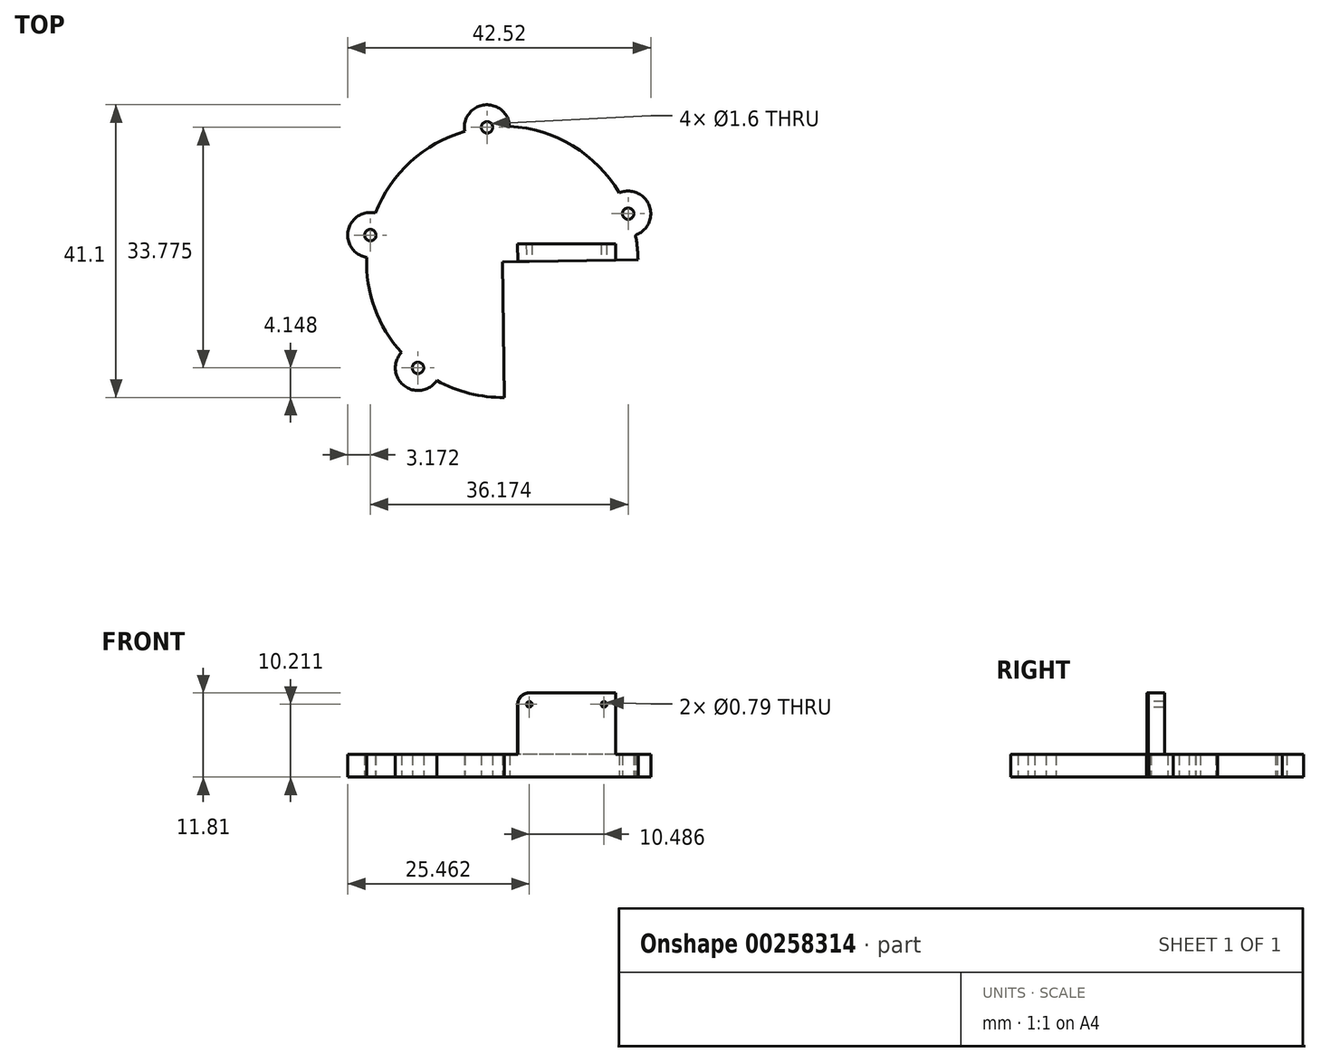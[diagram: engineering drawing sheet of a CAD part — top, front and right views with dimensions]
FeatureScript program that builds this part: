
annotation { "Feature Type Name" : "Feature", "Feature Type Description" : "" }
export const myFeature = defineFeature(function(context is Context, id is Id, definition is map)
    precondition{}
    {
        {
            var Q0;
            Q0=qCreatedBy(makeId("Top.planeOp"),FACE);
            var sketch = newSketch(context, id + "F0", { "sketchPlane" : qUnion([Q0])});
            skLineSegment(sketch, "E0", {"start": v(40.74, -31.1) * mm, "end": v(40.44, -12.05) * mm});
            skLineSegment(sketch, "E1", {"start": v(40.44, -12.05) * mm, "end": v(59.49, -11.75) * mm});
            skArc(sketch, "E2", {"start": v(59.49, -11.75) * mm, "mid": v(26.76, 1.2) * mm, "end": v(40.74, -31.1) * mm});
            skArc(sketch, "E3", {"start": v(26.28, -24.8) * mm, "mid": v(26.64, -29.44) * mm, "end": v(31.24, -28.73) * mm});
            skArc(sketch, "E4", {"start": v(22.66, -5.21) * mm, "mid": v(18.8, -7.67) * mm, "end": v(21.4, -11.43) * mm});
            skArc(sketch, "E5", {"start": v(41.47, 6.97) * mm, "mid": v(37.94, 9.98) * mm, "end": v(35.18, 6.26) * mm});
            skArc(sketch, "E6", {"start": v(59.12, -8.3) * mm, "mid": v(61.06, -4.16) * mm, "end": v(56.85, -2.38) * mm});
            skCircle(sketch, "E7", {"center": v(28.6, -26.95) * mm, "radius": 0.8 * mm});
            skCircle(sketch, "E8", {"center": v(21.92, -8.3) * mm, "radius": 0.8 * mm});
            skCircle(sketch, "E9", {"center": v(38.3, 6.82) * mm, "radius": 0.8 * mm});
            skCircle(sketch, "E10", {"center": v(58.1, -5.3) * mm, "radius": 0.8 * mm});
            skSolve(sketch);
        }
        {
            var Q0;
            Q0 = qSketchRegion(id + "F0", true);
            extrude(context, id + "F1", {"entities" : qUnion([Q0]), "depth" : 3.17 * mm});
        }
        {
            var Q0;
            Q0=makeQuery(id+"F1.opExtrude","CAP_FACE",FACE,{"disambiguationData":[OSD([sQuery(id+"F0.wireOp",EDGE,"E0"),sQuery(id+"F0.wireOp",EDGE,"E1"),sQuery(id+"F0.wireOp",EDGE,"E2"),sQuery(id+"F0.wireOp",EDGE,"E3"),sQuery(id+"F0.wireOp",EDGE,"E4"),sQuery(id+"F0.wireOp",EDGE,"E5"),sQuery(id+"F0.wireOp",EDGE,"E6"),sQuery(id+"F0.wireOp",EDGE,"E7"),sQuery(id+"F0.wireOp",EDGE,"E8"),sQuery(id+"F0.wireOp",EDGE,"E9"),sQuery(id+"F0.wireOp",EDGE,"E10")])],"isStart":false});
            var sketch = newSketch(context, id + "F2", { "sketchPlane" : qUnion([Q0])});
            skLineSegment(sketch, "E11.bottom", {"start": v(56.32, -11.8) * mm, "end": v(56.32, -11.8) * mm});
            skLineSegment(sketch, "E11.top", {"start": v(56.32, -9.56) * mm, "end": v(56.32, -9.56) * mm});
            skLineSegment(sketch, "E11.left", {"start": v(56.32, -11.8) * mm, "end": v(56.32, -9.56) * mm});
            skLineSegment(sketch, "E11.right", {"start": v(56.32, -11.8) * mm, "end": v(56.32, -9.56) * mm});
            skLineSegment(sketch, "E12", {"start": v(56.32, -9.56) * mm, "end": v(42.6, -9.56) * mm});
            skLineSegment(sketch, "E13", {"start": v(42.6, -9.56) * mm, "end": v(42.63, -12.02) * mm});
            skLineSegment(sketch, "E14", {"start": v(42.63, -12.02) * mm, "end": v(56.32, -11.8) * mm});
            skSolve(sketch);
        }
        {
            var Q0;
            Q0 = qSketchRegion(id + "F2", true);
            extrude(context, id + "F3", {"entities" : qUnion([Q0]), "operationType" : NewBodyOperationType.ADD, "depth" : 8.64 * mm});
        }
        {
            var Q0;
            Q0=makeQuery(id+"F3.opExtrude","CAP_EDGE",EDGE,{"disambiguationData":[OSD([sQuery(id+"F2.wireOp",EDGE,"E13")])],"isStart":false});
            var Q1;
            Q1=makeQuery(id+"F3.opExtrude","CAP_EDGE",EDGE,{"disambiguationData":[OSD([sQuery(id+"F2.wireOp",EDGE,"E11.right")])],"isStart":false});
            fillet(context, id + "F4", {"entities" : qUnion([Q0, Q1]), "radius" : 1.6 * mm, "tangentPropagation" : true, "allowEdgeOverflow" : false});
        }
        {
            var Q0;
            Q0=makeQuery(id+"F3.boolean.opBoolean","MERGE",FACE,{"derivedFrom":[makeQuery(id+"F1.opExtrude","SWEPT_FACE",FACE,{"disambiguationData":[OSD([sQuery(id+"F0.wireOp",EDGE,"E1")])]}),makeQuery(id+"F3.opExtrude","SWEPT_FACE",FACE,{"disambiguationData":[OSD([sQuery(id+"F2.wireOp",EDGE,"E14")])]})]});
            var sketch = newSketch(context, id + "F5", { "sketchPlane" : qUnion([Q0])});
            skCircle(sketch, "E15", {"center": v(44.04, 10.21) * mm, "radius": 0.4 * mm});
            skCircle(sketch, "E16", {"center": v(54.52, 10.21) * mm, "radius": 0.4 * mm});
            skSolve(sketch);
        }
        {
            var Q0;
            Q0=makeQuery(id+"F5.imprint","IMPRINT",FACE,{"disambiguationData":[TD([[makeQuery(id+"F5.imprint","IMPRINT",EDGE,{"derivedFrom":sQuery(id+"F5.wireOp",EDGE,"E15")}),1.0]])]});
            extrude(context, id + "F6", {"entities" : qUnion([Q0]), "operationType" : NewBodyOperationType.REMOVE, "oppositeDirection" : true, "depth" : 25.4 * mm});
        }
        {
            var Q0;
            Q0 = qSketchRegion(id + "F5", true);
            extrude(context, id + "F7", {"entities" : qUnion([Q0]), "operationType" : NewBodyOperationType.REMOVE, "oppositeDirection" : true, "depth" : 25.4 * mm});
        }
    });
